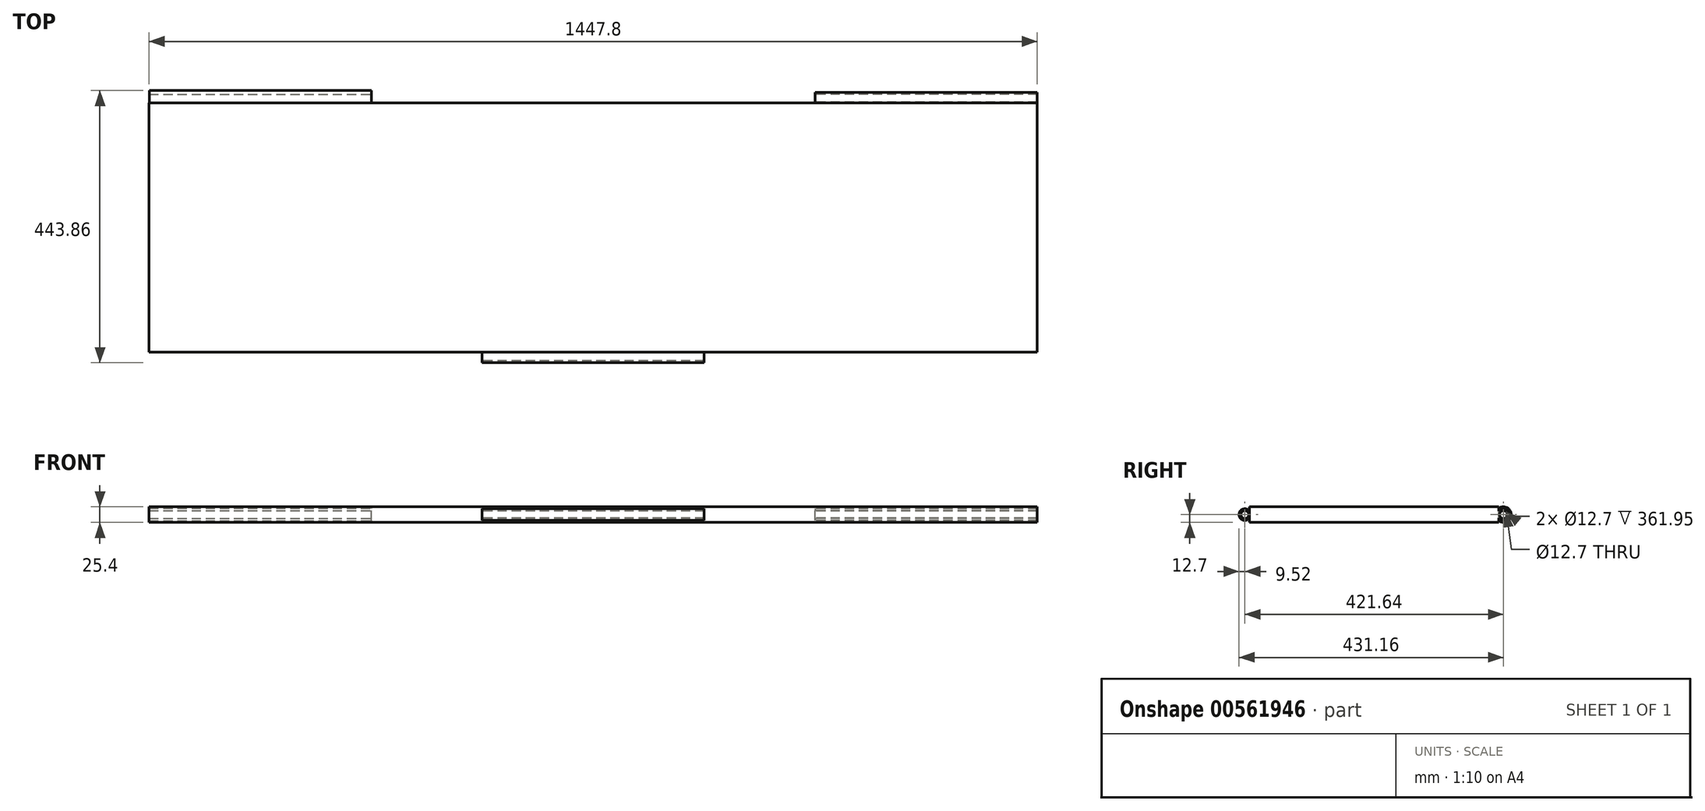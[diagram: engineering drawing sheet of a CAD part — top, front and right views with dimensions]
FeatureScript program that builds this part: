
annotation { "Feature Type Name" : "Feature", "Feature Type Description" : "" }
export const myFeature = defineFeature(function(context is Context, id is Id, definition is map)
    precondition{}
    {
        {
            var Q0;
            Q0=qCreatedBy(makeId("Top.planeOp"),FACE);
            var sketch = newSketch(context, id + "F0", { "sketchPlane" : qUnion([Q0])});
            skLineSegment(sketch, "E0.bottom", {"start": v(723.9, 203.2) * mm, "end": v(-723.9, 203.2) * mm});
            skLineSegment(sketch, "E0.top", {"start": v(723.9, -203.2) * mm, "end": v(-723.9, -203.2) * mm});
            skLineSegment(sketch, "E0.left", {"start": v(723.9, 203.2) * mm, "end": v(723.9, -203.2) * mm});
            skLineSegment(sketch, "E0.right", {"start": v(-723.9, 203.2) * mm, "end": v(-723.9, -203.2) * mm});
            skPoint(sketch, "E0.middle", {"position": v(0, 0) * mm});
            skSolve(sketch);
        }
        {
            var Q0;
            Q0=qCreatedBy(makeId("Right.planeOp"),FACE);
            var sketch = newSketch(context, id + "F1", { "sketchPlane" : qUnion([Q0])});
            skCircle(sketch, "E1", {"center": v(-210.82, 0) * mm, "radius": 9.53 * mm});
            skCircle(sketch, "E2", {"center": v(-210.82, 0) * mm, "radius": 6.35 * mm});
            skSolve(sketch);
        }
        {
            var Q0;
            Q0=qCreatedBy(makeId("Right.planeOp"),FACE);
            cPlane(context, id + "F2", {"entities" : qUnion([Q0]), "cplaneType" : CPlaneType.OFFSET, "offset" : 361.95 * mm, "width" : 152.4 * mm, "height" : 152.4 * mm});
        }
        {
            var Q0;
            Q0=qCreatedBy(makeId("Right.planeOp"),FACE);
            cPlane(context, id + "F3", {"entities" : qUnion([Q0]), "cplaneType" : CPlaneType.OFFSET, "offset" : 361.7 * mm, "oppositeDirection" : true, "width" : 152.4 * mm, "height" : 152.4 * mm});
        }
        {
            var Q0;
            Q0=qCreatedBy(id+"F3.planeOp",FACE);
            var sketch = newSketch(context, id + "F4", { "sketchPlane" : qUnion([Q0])});
            skCircle(sketch, "E3", {"center": v(210.82, 0) * mm, "radius": 12.7 * mm});
            skCircle(sketch, "E4", {"center": v(210.82, 0) * mm, "radius": 6.35 * mm});
            skSolve(sketch);
        }
        {
            var Q0;
            Q0=qCreatedBy(id+"F2.planeOp",FACE);
            var sketch = newSketch(context, id + "F5", { "sketchPlane" : qUnion([Q0])});
            skCircle(sketch, "E5", {"center": v(210.82, 0) * mm, "radius": 9.53 * mm});
            skCircle(sketch, "E6", {"center": v(210.82, 0) * mm, "radius": 6.35 * mm});
            skSolve(sketch);
        }
        {
            var Q0;
            Q0=makeQuery(id+"F0.imprint","IMPRINT",FACE,{"disambiguationData":[TD([[makeQuery(id+"F0.imprint","IMPRINT",EDGE,{"derivedFrom":sQuery(id+"F0.wireOp",EDGE,"E0.bottom")}),1.0]])]});
            extrude(context, id + "F6", {"entities" : qUnion([Q0]), "depth" : 25.4 * mm, "offsetDistance" : 25.4 * mm, "symmetric" : true});
        }
        {
            var Q0;
            Q0=makeQuery(id+"F1.imprint","IMPRINT",FACE,{"disambiguationData":[TD([[makeQuery(id+"F1.imprint","IMPRINT",EDGE,{"derivedFrom":sQuery(id+"F1.wireOp",EDGE,"E1")}),1.0]])]});
            extrude(context, id + "F7", {"entities" : qUnion([Q0]), "operationType" : NewBodyOperationType.ADD, "depth" : 361.95 * mm, "offsetDistance" : 25.4 * mm, "symmetric" : true});
        }
        {
            var Q0;
            Q0=makeQuery(id+"F5.imprint","IMPRINT",FACE,{"disambiguationData":[TD([[makeQuery(id+"F5.imprint","IMPRINT",EDGE,{"derivedFrom":sQuery(id+"F5.wireOp",EDGE,"E5")}),1.0]])]});
            extrude(context, id + "F8", {"entities" : qUnion([Q0]), "operationType" : NewBodyOperationType.ADD, "depth" : 361.95 * mm, "offsetDistance" : 25.4 * mm});
        }
        {
            var Q0;
            Q0=makeQuery(id+"F4.imprint","IMPRINT",FACE,{"disambiguationData":[TD([[makeQuery(id+"F4.imprint","IMPRINT",EDGE,{"derivedFrom":sQuery(id+"F4.wireOp",EDGE,"E3")}),1.0]])]});
            extrude(context, id + "F9", {"entities" : qUnion([Q0]), "operationType" : NewBodyOperationType.ADD, "oppositeDirection" : true, "depth" : 361.95 * mm, "offsetDistance" : 25.4 * mm});
        }
    });
